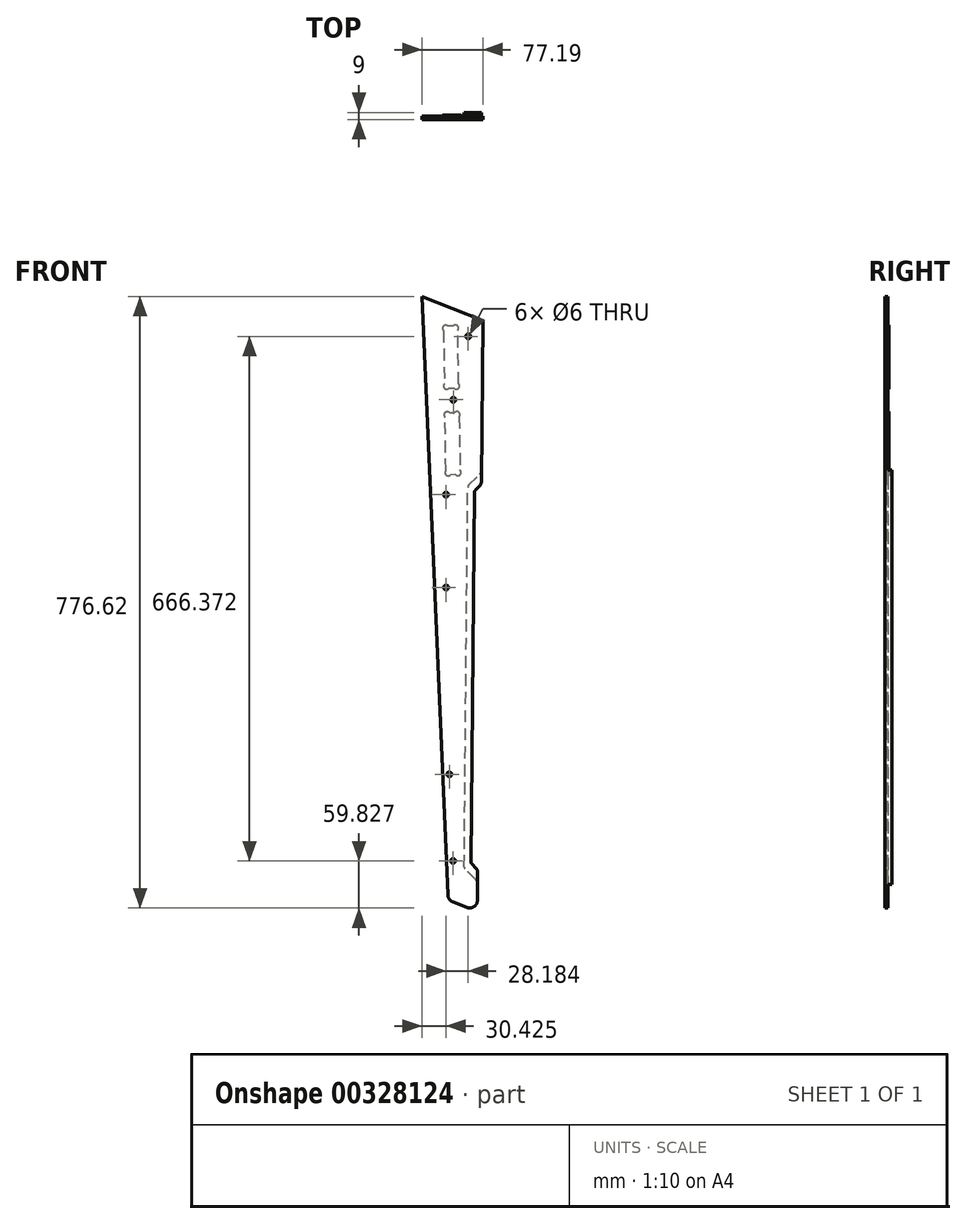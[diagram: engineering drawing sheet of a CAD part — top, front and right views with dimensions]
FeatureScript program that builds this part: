
annotation { "Feature Type Name" : "Feature", "Feature Type Description" : "" }
export const myFeature = defineFeature(function(context is Context, id is Id, definition is map)
    precondition{}
    {
        {
            var Q0;
            Q0=qCreatedBy(makeId("Front.planeOp"),FACE);
            var sketch = newSketch(context, id + "F0", { "sketchPlane" : qUnion([Q0])});
            skArc(sketch, "E0", {"start": v(-55.36, -345.94) * mm, "mid": v(-46.11, -344.91) * mm, "end": v(-41.72, -336.72) * mm});
            skLineSegment(sketch, "E1", {"start": v(-41.72, -336.72) * mm, "end": v(-34.9, 399.8) * mm});
            skLineSegment(sketch, "E2", {"start": v(-34.9, 399.8) * mm, "end": v(-112.09, 429.99) * mm});
            skLineSegment(sketch, "E3", {"start": v(-112.09, 429.99) * mm, "end": v(-79.3, -330.18) * mm});
            skArc(sketch, "E4", {"start": v(-79.3, -330.18) * mm, "mid": v(-77.45, -335.56) * mm, "end": v(-72.95, -339.06) * mm});
            skLineSegment(sketch, "E5", {"start": v(-72.95, -339.06) * mm, "end": v(-55.36, -345.94) * mm});
            skCircle(sketch, "E6", {"center": v(-81.67, 178.45) * mm, "radius": 3 * mm});
            skCircle(sketch, "E7", {"center": v(-81.55, 60.4) * mm, "radius": 3 * mm});
            skCircle(sketch, "E8", {"center": v(-53.48, 379.57) * mm, "radius": 3 * mm});
            skCircle(sketch, "E9", {"center": v(-72.34, 298.97) * mm, "radius": 3 * mm});
            skCircle(sketch, "E10", {"center": v(-72.76, -286.8) * mm, "radius": 3 * mm});
            skCircle(sketch, "E11", {"center": v(-77.5, -176.9) * mm, "radius": 3 * mm});
            skArc(sketch, "E12", {"start": v(-83.71, 319.13) * mm, "mid": v(-83.62, 313.47) * mm, "end": v(-77.96, 313.57) * mm});
            skLineSegment(sketch, "E13", {"start": v(-77.96, 313.57) * mm, "end": v(-71.27, 313.68) * mm});
            skArc(sketch, "E14", {"start": v(-71.27, 313.68) * mm, "mid": v(-65.62, 313.78) * mm, "end": v(-65.71, 319.43) * mm});
            skLineSegment(sketch, "E15", {"start": v(-65.71, 319.43) * mm, "end": v(-66.86, 387.1) * mm});
            skArc(sketch, "E16", {"start": v(-66.86, 387.1) * mm, "mid": v(-66.96, 392.76) * mm, "end": v(-72.61, 392.67) * mm});
            skLineSegment(sketch, "E17", {"start": v(-72.61, 392.67) * mm, "end": v(-79.3, 392.56) * mm});
            skArc(sketch, "E18", {"start": v(-79.3, 392.56) * mm, "mid": v(-84.95, 392.46) * mm, "end": v(-84.86, 386.8) * mm});
            skLineSegment(sketch, "E19", {"start": v(-84.86, 386.8) * mm, "end": v(-83.71, 319.13) * mm});
            skLineSegment(sketch, "E20", {"start": v(-69.41, 203.7) * mm, "end": v(-76.1, 203.58) * mm});
            skArc(sketch, "E21", {"start": v(-76.1, 203.58) * mm, "mid": v(-81.75, 203.49) * mm, "end": v(-81.85, 209.14) * mm});
            skLineSegment(sketch, "E22", {"start": v(-81.85, 209.14) * mm, "end": v(-83, 276.82) * mm});
            skArc(sketch, "E23", {"start": v(-83, 276.82) * mm, "mid": v(-83.1, 282.48) * mm, "end": v(-77.44, 282.57) * mm});
            skLineSegment(sketch, "E24", {"start": v(-77.44, 282.57) * mm, "end": v(-70.75, 282.69) * mm});
            skArc(sketch, "E25", {"start": v(-70.75, 282.69) * mm, "mid": v(-65.1, 282.78) * mm, "end": v(-65, 277.13) * mm});
            skLineSegment(sketch, "E26", {"start": v(-65, 277.13) * mm, "end": v(-63.85, 209.45) * mm});
            skArc(sketch, "E27", {"start": v(-63.85, 209.45) * mm, "mid": v(-63.76, 203.8) * mm, "end": v(-69.41, 203.7) * mm});
            skArc(sketch, "E28", {"start": v(-32, -319.55) * mm, "mid": v(-36.82, -324.29) * mm, "end": v(-41.56, -319.46) * mm});
            skLineSegment(sketch, "E29", {"start": v(-41.56, -319.46) * mm, "end": v(-41.53, -316.78) * mm});
            skArc(sketch, "E30", {"start": v(-41.53, -316.78) * mm, "mid": v(-42.11, -313.71) * mm, "end": v(-43.82, -311.1) * mm});
            skLineSegment(sketch, "E31", {"start": v(-43.82, -311.1) * mm, "end": v(-57.4, -297.27) * mm});
            skArc(sketch, "E32", {"start": v(-57.4, -297.27) * mm, "mid": v(-58.25, -295.97) * mm, "end": v(-58.54, -294.44) * mm});
            skLineSegment(sketch, "E33", {"start": v(-58.54, -294.44) * mm, "end": v(-54.07, 187.8) * mm});
            skArc(sketch, "E34", {"start": v(-54.07, 187.8) * mm, "mid": v(-53.76, 189.33) * mm, "end": v(-52.88, 190.62) * mm});
            skLineSegment(sketch, "E35", {"start": v(-52.88, 190.62) * mm, "end": v(-39.05, 204.2) * mm});
            skArc(sketch, "E36", {"start": v(-39.05, 204.2) * mm, "mid": v(-37.3, 206.77) * mm, "end": v(-36.66, 209.83) * mm});
            skLineSegment(sketch, "E37", {"start": v(-36.66, 209.83) * mm, "end": v(-36.63, 212.51) * mm});
            skArc(sketch, "E38", {"start": v(-36.63, 212.51) * mm, "mid": v(-31.8, 217.25) * mm, "end": v(-27.07, 212.42) * mm});
            skLineSegment(sketch, "E39", {"start": v(-27.07, 212.42) * mm, "end": v(-32, -319.55) * mm});
            skArc(sketch, "E40", {"start": v(-43.68, -296.1) * mm, "mid": v(-41.97, -298.71) * mm, "end": v(-41.4, -301.78) * mm});
            skLineSegment(sketch, "E41", {"start": v(-41.4, -301.78) * mm, "end": v(-41.42, -304.47) * mm});
            skArc(sketch, "E42", {"start": v(-41.42, -304.47) * mm, "mid": v(-36.68, -309.3) * mm, "end": v(-31.85, -304.55) * mm});
            skLineSegment(sketch, "E43", {"start": v(-31.85, -304.55) * mm, "end": v(-27.2, 197.42) * mm});
            skArc(sketch, "E44", {"start": v(-27.2, 197.42) * mm, "mid": v(-31.94, 202.25) * mm, "end": v(-36.77, 197.51) * mm});
            skLineSegment(sketch, "E45", {"start": v(-36.77, 197.51) * mm, "end": v(-36.8, 194.83) * mm});
            skArc(sketch, "E46", {"start": v(-36.8, 194.83) * mm, "mid": v(-37.43, 191.77) * mm, "end": v(-39.19, 189.2) * mm});
            skLineSegment(sketch, "E47", {"start": v(-39.19, 189.2) * mm, "end": v(-44.33, 184.15) * mm});
            skArc(sketch, "E48", {"start": v(-44.33, 184.15) * mm, "mid": v(-45.2, 182.86) * mm, "end": v(-45.53, 181.33) * mm});
            skLineSegment(sketch, "E49", {"start": v(-45.53, 181.33) * mm, "end": v(-49.87, -288.12) * mm});
            skArc(sketch, "E50", {"start": v(-49.87, -288.12) * mm, "mid": v(-49.58, -289.66) * mm, "end": v(-48.73, -290.96) * mm});
            skLineSegment(sketch, "E51", {"start": v(-48.73, -290.96) * mm, "end": v(-43.68, -296.1) * mm});
            skSolve(sketch);
        }
        {
            var Q0;
            Q0=makeQuery(id+"F0.imprint","IMPRINT",FACE,{"disambiguationData":[TD([[makeQuery(id+"F0.imprint","IMPRINT",EDGE,{"derivedFrom":sQuery(id+"F0.wireOp",EDGE,"E10")}),-1.0]])]});
            var Q1;
            Q1=makeQuery(id+"F0.imprint","IMPRINT",FACE,{"disambiguationData":[TD([[makeQuery(id+"F0.imprint","IMPRINT",EDGE,{"derivedFrom":sQuery(id+"F0.wireOp",EDGE,"E11")}),-1.0]])]});
            var Q2;
            Q2=makeQuery(id+"F0.imprint","IMPRINT",FACE,{"disambiguationData":[TD([[makeQuery(id+"F0.imprint","IMPRINT",EDGE,{"derivedFrom":sQuery(id+"F0.wireOp",EDGE,"E7")}),-1.0]])]});
            var Q3;
            Q3=makeQuery(id+"F0.imprint","IMPRINT",FACE,{"disambiguationData":[TD([[makeQuery(id+"F0.imprint","IMPRINT",EDGE,{"derivedFrom":sQuery(id+"F0.wireOp",EDGE,"E6")}),-1.0]])]});
            var Q4;
            {var subQ2=sQuery(id+"F0.wireOp",EDGE,"E0");Q4=makeQuery(id+"F0.imprint","IMPRINT",FACE,{"disambiguationData":[TD([[makeQuery(id+"F0.imprint","IMPRINT",EDGE,{"derivedFrom":subQ2}),1.0]])]});}
            var Q5;
            Q5=makeQuery(id+"F0.imprint","IMPRINT",FACE,{"disambiguationData":[TD([[makeQuery(id+"F0.imprint","IMPRINT",EDGE,{"derivedFrom":sQuery(id+"F0.wireOp",EDGE,"E8")}),-1.0]])]});
            var Q6;
            Q6=makeQuery(id+"F0.imprint","IMPRINT",FACE,{"disambiguationData":[TD([[makeQuery(id+"F0.imprint","IMPRINT",EDGE,{"derivedFrom":sQuery(id+"F0.wireOp",EDGE,"E9")}),-1.0]])]});
            var Q7;
            {var subQ3=sQuery(id+"F0.wireOp",EDGE,"E30");Q7=makeQuery(id+"F0.imprint","IMPRINT",FACE,{"disambiguationData":[TD([[makeQuery(id+"F0.imprint","IMPRINT",EDGE,{"derivedFrom":subQ3}),-1.0]])]});}
            var Q8;
            {var subQ1=sQuery(id+"F0.wireOp",EDGE,"E40");Q8=makeQuery(id+"F0.imprint","IMPRINT",FACE,{"disambiguationData":[TD([[makeQuery(id+"F0.imprint","IMPRINT",EDGE,{"derivedFrom":subQ1}),1.0]])]});}
            var Q9;
            Q9=makeQuery(id+"F0.imprint","IMPRINT",FACE,{"disambiguationData":[TD([[makeQuery(id+"F0.imprint","IMPRINT",EDGE,{"derivedFrom":sQuery(id+"F0.wireOp",EDGE,"E20")}),-1.0]])]});
            var Q10;
            Q10=makeQuery(id+"F0.imprint","IMPRINT",FACE,{"disambiguationData":[TD([[makeQuery(id+"F0.imprint","IMPRINT",EDGE,{"derivedFrom":sQuery(id+"F0.wireOp",EDGE,"E12")}),1.0]])]});
            extrude(context, id + "F1", {"entities" : qUnion([Q0, Q1, Q2, Q3, Q4, Q5, Q6, Q7, Q8, Q9, Q10]), "depth" : 18 * mm});
        }
        {
            var Q0;
            Q0=makeQuery(id+"F0.imprint","IMPRINT",FACE,{"disambiguationData":[TD([[makeQuery(id+"F0.imprint","IMPRINT",EDGE,{"derivedFrom":sQuery(id+"F0.wireOp",EDGE,"E10")}),-1.0]])]});
            var Q1;
            Q1=makeQuery(id+"F0.imprint","IMPRINT",FACE,{"disambiguationData":[TD([[makeQuery(id+"F0.imprint","IMPRINT",EDGE,{"derivedFrom":sQuery(id+"F0.wireOp",EDGE,"E11")}),-1.0]])]});
            var Q2;
            Q2=makeQuery(id+"F0.imprint","IMPRINT",FACE,{"disambiguationData":[TD([[makeQuery(id+"F0.imprint","IMPRINT",EDGE,{"derivedFrom":sQuery(id+"F0.wireOp",EDGE,"E7")}),-1.0]])]});
            var Q3;
            Q3=makeQuery(id+"F0.imprint","IMPRINT",FACE,{"disambiguationData":[TD([[makeQuery(id+"F0.imprint","IMPRINT",EDGE,{"derivedFrom":sQuery(id+"F0.wireOp",EDGE,"E6")}),-1.0]])]});
            var Q4;
            Q4=makeQuery(id+"F0.imprint","IMPRINT",FACE,{"disambiguationData":[TD([[makeQuery(id+"F0.imprint","IMPRINT",EDGE,{"derivedFrom":sQuery(id+"F0.wireOp",EDGE,"E9")}),-1.0]])]});
            var Q5;
            Q5=makeQuery(id+"F0.imprint","IMPRINT",FACE,{"disambiguationData":[TD([[makeQuery(id+"F0.imprint","IMPRINT",EDGE,{"derivedFrom":sQuery(id+"F0.wireOp",EDGE,"E8")}),-1.0]])]});
            extrude(context, id + "F2", {"entities" : qUnion([Q0, Q1, Q2, Q3, Q4, Q5]), "operationType" : NewBodyOperationType.REMOVE, "depth" : 14 * mm});
        }
        {
            var Q0;
            {var subQ1=sQuery(id+"F0.wireOp",EDGE,"E40");Q0=makeQuery(id+"F0.imprint","IMPRINT",FACE,{"disambiguationData":[TD([[makeQuery(id+"F0.imprint","IMPRINT",EDGE,{"derivedFrom":subQ1}),1.0]])]});}
            extrude(context, id + "F3", {"entities" : qUnion([Q0]), "operationType" : NewBodyOperationType.REMOVE, "depth" : 9 * mm});
        }
        {
            var Q0;
            {var subQ3=sQuery(id+"F0.wireOp",EDGE,"E30");Q0=makeQuery(id+"F0.imprint","IMPRINT",FACE,{"disambiguationData":[TD([[makeQuery(id+"F0.imprint","IMPRINT",EDGE,{"derivedFrom":subQ3}),-1.0]])]});}
            extrude(context, id + "F4", {"entities" : qUnion([Q0]), "operationType" : NewBodyOperationType.REMOVE, "depth" : 6 * mm});
        }
        {
            var Q0;
            Q0=makeQuery(id+"F0.imprint","IMPRINT",FACE,{"disambiguationData":[TD([[makeQuery(id+"F0.imprint","IMPRINT",EDGE,{"derivedFrom":sQuery(id+"F0.wireOp",EDGE,"E20")}),-1.0]])]});
            var Q1;
            Q1=makeQuery(id+"F0.imprint","IMPRINT",FACE,{"disambiguationData":[TD([[makeQuery(id+"F0.imprint","IMPRINT",EDGE,{"derivedFrom":sQuery(id+"F0.wireOp",EDGE,"E12")}),1.0]])]});
            extrude(context, id + "F5", {"entities" : qUnion([Q0, Q1]), "operationType" : NewBodyOperationType.REMOVE, "depth" : 12.5 * mm});
        }
    });
